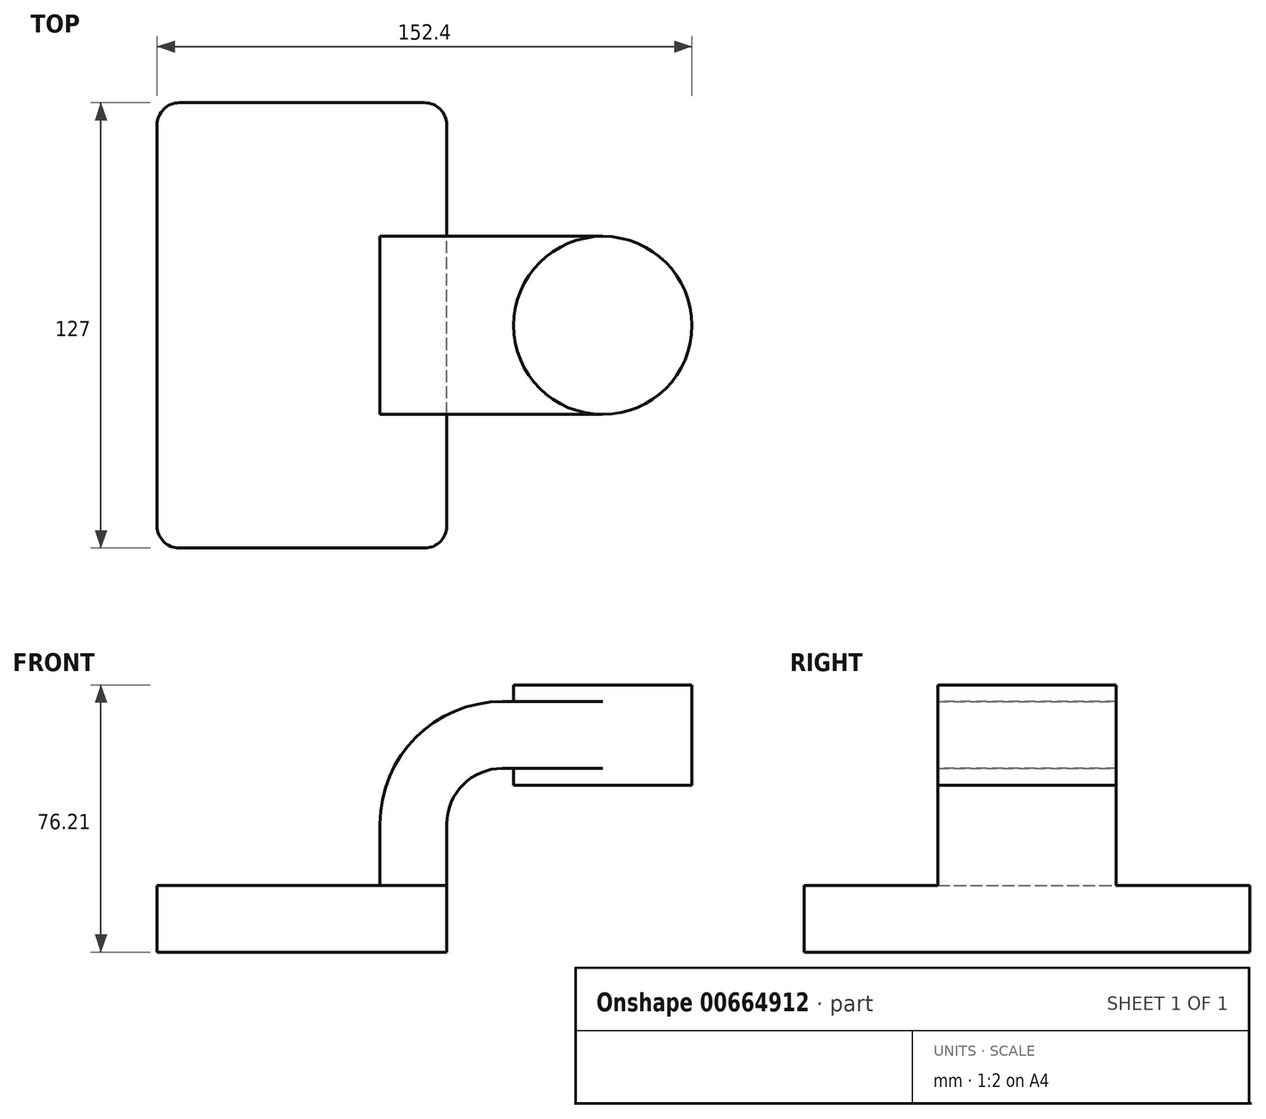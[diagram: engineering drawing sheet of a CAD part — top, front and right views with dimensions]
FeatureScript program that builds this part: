
annotation { "Feature Type Name" : "Feature", "Feature Type Description" : "" }
export const myFeature = defineFeature(function(context is Context, id is Id, definition is map)
    precondition{}
    {
        {
            var Q0;
            Q0=qCreatedBy(makeId("Front.planeOp"),FACE);
            var sketch = newSketch(context, id + "F0", { "sketchPlane" : qUnion([Q0])});
            skLineSegment(sketch, "E0.bottom", {"start": v(41.28, -9.52) * mm, "end": v(-41.28, -9.53) * mm});
            skLineSegment(sketch, "E0.top", {"start": v(41.27, 9.53) * mm, "end": v(-41.28, 9.53) * mm});
            skLineSegment(sketch, "E0.left", {"start": v(41.28, -9.52) * mm, "end": v(41.28, 9.53) * mm});
            skLineSegment(sketch, "E0.right", {"start": v(-41.28, -9.53) * mm, "end": v(-41.28, 9.53) * mm});
            skPoint(sketch, "E0.middle", {"position": v(0, 0) * mm});
            skLineSegment(sketch, "E1", {"start": v(41.27, 9.53) * mm, "end": v(41.27, 27) * mm});
            skArc(sketch, "E2", {"start": v(41.28, 27) * mm, "mid": v(45.92, 38.23) * mm, "end": v(57.15, 42.88) * mm});
            skLineSegment(sketch, "E3.bottom", {"start": v(111.13, 38.1) * mm, "end": v(60.33, 38.1) * mm});
            skLineSegment(sketch, "E3.top", {"start": v(111.13, 66.68) * mm, "end": v(60.33, 66.68) * mm});
            skLineSegment(sketch, "E3.left", {"start": v(111.13, 38.1) * mm, "end": v(111.13, 66.68) * mm});
            skLineSegment(sketch, "E3.right", {"start": v(60.33, 38.1) * mm, "end": v(60.33, 66.68) * mm});
            skPoint(sketch, "E3.middle", {"position": v(85.73, 52.39) * mm});
            skLineSegment(sketch, "E4", {"start": v(57.15, 42.88) * mm, "end": v(85.73, 42.88) * mm});
            skLineSegment(sketch, "E5.0", {"start": v(57.15, 61.93) * mm, "end": v(85.73, 61.93) * mm});
            skArc(sketch, "E5.1", {"start": v(22.22, 27) * mm, "mid": v(32.45, 51.7) * mm, "end": v(57.15, 61.93) * mm});
            skLineSegment(sketch, "E5.2", {"start": v(22.22, 9.53) * mm, "end": v(22.22, 27) * mm});
            skLineSegment(sketch, "E6", {"start": v(85.73, 66.68) * mm, "end": v(85.73, 61.93) * mm});
            skLineSegment(sketch, "E7", {"start": v(85.73, 52.39) * mm, "end": v(85.73, 42.88) * mm});
            skLineSegment(sketch, "E8", {"start": v(85.73, 61.93) * mm, "end": v(85.72, 52.39) * mm});
            skLineSegment(sketch, "E9", {"start": v(85.72, 42.88) * mm, "end": v(85.73, 38.1) * mm});
            skFitSpline(sketch, "E10", {"points": [v(-41.28, 9.52) * mm, v(57.15, 61.93) * mm], "startDerivative": vector(28.42, 89.28) * mm, "endDerivative": vector(140.54, -7.9) * mm});
            skSolve(sketch);
        }
        {
            var Q0;
            Q0=makeQuery(id+"F0.imprint","IMPRINT",FACE,{"disambiguationData":[TD([[makeQuery(id+"F0.imprint","IMPRINT",EDGE,{"derivedFrom":sQuery(id+"F0.wireOp",EDGE,"E0.bottom")}),-1.0]])]});
            extrude(context, id + "F1", {"entities" : qUnion([Q0]), "endBound" : BoundingType.SYMMETRIC, "depth" : 127 * mm, "offsetDistance" : 25.4 * mm});
        }
        {
            var Q0;
            {var subQ5=sQuery(id+"F0.wireOp",EDGE,"E1");Q0=makeQuery(id+"F0.imprint","IMPRINT",FACE,{"disambiguationData":[TD([[makeQuery(id+"F0.imprint","IMPRINT",EDGE,{"derivedFrom":subQ5}),1.0]])]});}
            var Q1;
            {var subQ0=sQuery(id+"F0.wireOp",EDGE,"E7");Q1=makeQuery(id+"F0.imprint","IMPRINT",FACE,{"disambiguationData":[TD([[makeQuery(id+"F0.imprint","IMPRINT",EDGE,{"derivedFrom":subQ0}),-1.0]])]});}
            extrude(context, id + "F2", {"entities" : qUnion([Q0, Q1]), "operationType" : NewBodyOperationType.ADD, "endBound" : BoundingType.SYMMETRIC, "depth" : 50.8 * mm, "offsetDistance" : 25.4 * mm});
        }
        {
            var Q0;
            Q0=makeQuery(id+"F0.imprint","IMPRINT",FACE,{"disambiguationData":[TD([[makeQuery(id+"F0.imprint","IMPRINT",EDGE,{"derivedFrom":sQuery(id+"F0.wireOp",EDGE,"E5.1")}),1.0]])]});
            extrude(context, id + "F3", {"entities" : qUnion([Q0]), "operationType" : NewBodyOperationType.ADD, "endBound" : BoundingType.SYMMETRIC, "depth" : 15.88 * mm, "offsetDistance" : 25.4 * mm});
        }
        {
            var Q0;
            {var subQ1=sQuery(id+"F0.wireOp",EDGE,"E3.left");Q0=makeQuery(id+"F0.imprint","IMPRINT",FACE,{"disambiguationData":[TD([[makeQuery(id+"F0.imprint","IMPRINT",EDGE,{"derivedFrom":subQ1}),1.0]])]});}
            var Q1;
            Q1=sQuery(id+"F0.wireOp",EDGE,"E8");
            revolve(context, id + "F4", {"operationType" : NewBodyOperationType.ADD, "entities" : qUnion([Q0]), "axis" : qUnion([Q1]), "revolveType" : RevolveType.FULL});
        }
        {
            var Q0;
            Q0=makeQuery(id+"F1.opExtrude","CAP_EDGE",EDGE,{"disambiguationData":[OSD([sQuery(id+"F0.wireOp",EDGE,"E0.right")])],"isStart":false});
            var Q1;
            Q1=makeQuery(id+"F1.opExtrude","CAP_EDGE",EDGE,{"disambiguationData":[OSD([sQuery(id+"F0.wireOp",EDGE,"E0.left")])],"isStart":false});
            var Q2;
            Q2=makeQuery(id+"F1.opExtrude","CAP_EDGE",EDGE,{"disambiguationData":[OSD([sQuery(id+"F0.wireOp",EDGE,"E0.left")])],"isStart":true});
            var Q3;
            Q3=makeQuery(id+"F1.opExtrude","CAP_EDGE",EDGE,{"disambiguationData":[OSD([sQuery(id+"F0.wireOp",EDGE,"E0.right")])],"isStart":true});
            fillet(context, id + "F5", {"entities" : qUnion([Q0, Q1, Q2, Q3]), "radius" : 6.35 * mm, "tangentPropagation" : true, "allowEdgeOverflow" : false});
        }
    });
